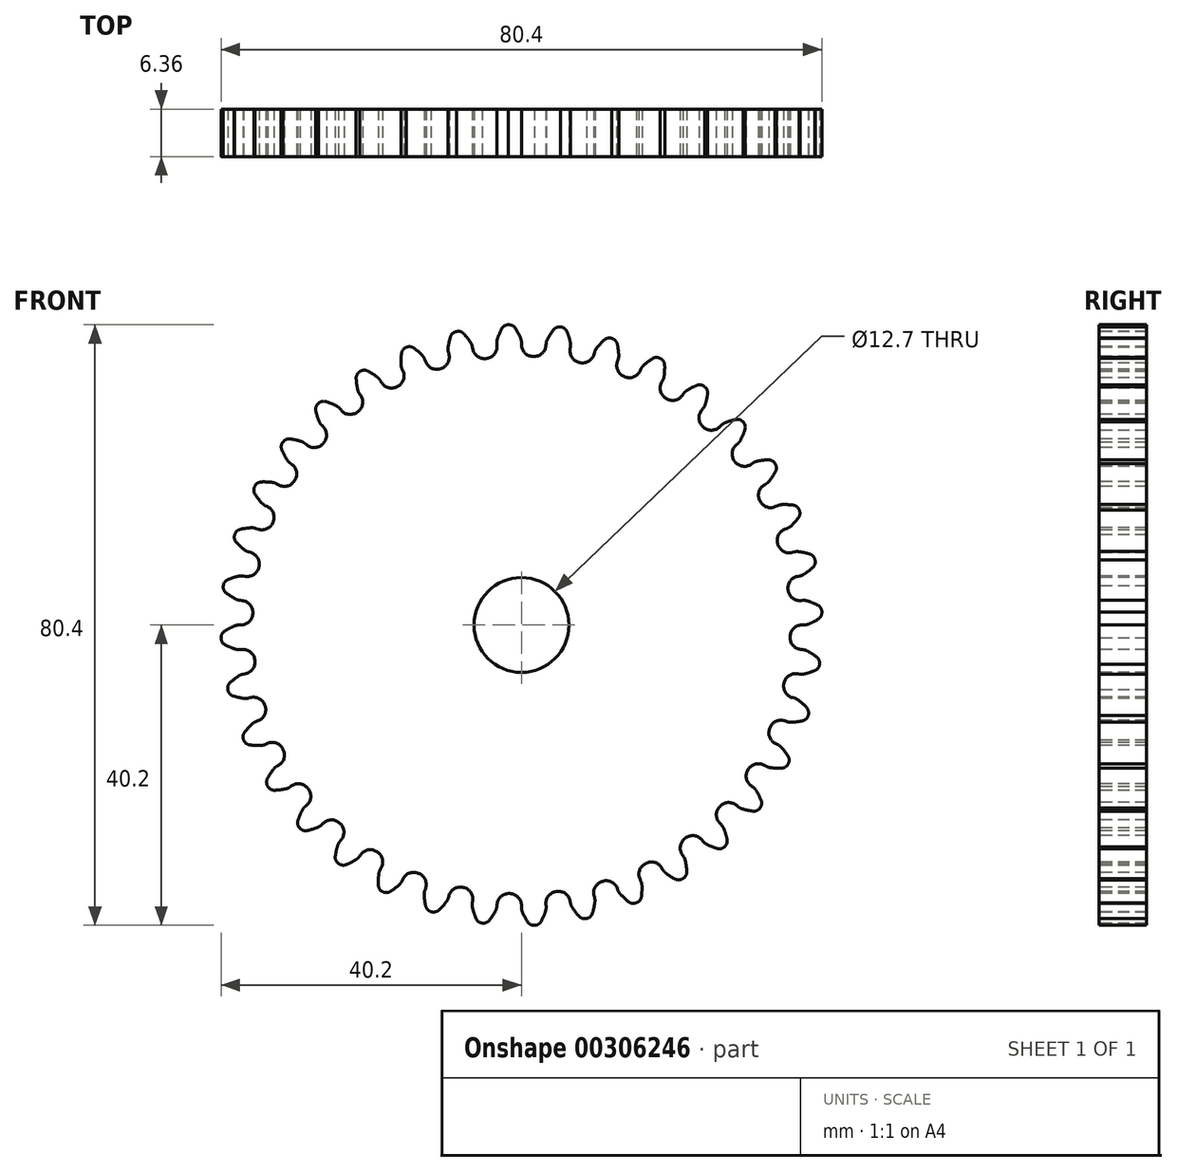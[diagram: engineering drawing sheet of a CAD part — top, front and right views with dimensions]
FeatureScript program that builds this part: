
annotation { "Feature Type Name" : "Feature", "Feature Type Description" : "" }
export const myFeature = defineFeature(function(context is Context, id is Id, definition is map)
    precondition{}
    {
        {
            var Q0;
            Q0=qCreatedBy(makeId("Front.planeOp"),FACE);
            var sketch = newSketch(context, id + "F0", { "sketchPlane" : qUnion([Q0])});
            skCircle(sketch, "E0", {"center": v(0, 0) * mm, "radius": 35.98 * mm});
            skSolve(sketch);
        }
        {
            var Q0;
            Q0 = qSketchRegion(id + "F0", true);
            extrude(context, id + "F1", {"entities" : qUnion([Q0]), "depth" : 3.17 * mm});
        }
        {
            var Q0;
            Q0=makeQuery(id+"F1.opExtrude","CAP_FACE",FACE,{"disambiguationData":[OSD([sQuery(id+"F0.wireOp",EDGE,"E0")])],"isStart":true});
            extrude(context, id + "F2", {"entities" : qUnion([Q0]), "operationType" : NewBodyOperationType.ADD, "depth" : 3.17 * mm});
        }
        {
            var Q0;
            Q0=makeQuery(id+"F1.opExtrude","CAP_FACE",FACE,{"disambiguationData":[OSD([sQuery(id+"F0.wireOp",EDGE,"E0")])],"isStart":false});
            var sketch = newSketch(context, id + "F3", { "sketchPlane" : qUnion([Q0])});
            skArc(sketch, "E1", {"start": v(-4.65, 35.68) * mm, "mid": v(1.57, -35.95) * mm, "end": v(1.52, 35.95) * mm});
            skArc(sketch, "E2.trimOffspring", {"start": v(-0.13, 38.41) * mm, "mid": v(-0.44, 39.08) * mm, "end": v(-0.8, 39.72) * mm});
            skLineSegment(sketch, "E3", {"start": v(-1.67, 40.2) * mm, "end": v(-1.76, 40.2) * mm});
            skLineSegment(sketch, "E4", {"start": v(0, 37.8) * mm, "end": v(0, 37.54) * mm});
            skLineSegment(sketch, "E5.MirrorCS", {"start": v(-1.84, 40.2) * mm, "end": v(-1.76, 40.2) * mm});
            skArc(sketch, "E6.MirrorCS", {"start": v(-3.22, 38.28) * mm, "mid": v(-2.97, 38.97) * mm, "end": v(-2.66, 39.64) * mm});
            skLineSegment(sketch, "E7.MirrorCS", {"start": v(-3.3, 37.65) * mm, "end": v(-3.27, 37.4) * mm});
            skPoint(sketch, "E8.orphan", {"position": v(-3.03, 34.61) * mm});
            skPoint(sketch, "E9.orphan", {"position": v(0, 34.74) * mm});
            skPoint(sketch, "E10.visualSharp", {"position": v(0, 35.98) * mm});
            skArc(sketch, "E10.filletArc", {"start": v(0, 36.45) * mm, "mid": v(0.13, 36.12) * mm, "end": v(0.46, 35.98) * mm});
            skArc(sketch, "E11.filletArc", {"start": v(0, 37.54) * mm, "mid": v(0.44, 36.44) * mm, "end": v(1.52, 35.95) * mm});
            skPoint(sketch, "E12.visualSharp", {"position": v(-3.14, 35.85) * mm});
            skArc(sketch, "E12.filletArc", {"start": v(-4.65, 35.68) * mm, "mid": v(-3.62, 36.26) * mm, "end": v(-3.27, 37.4) * mm});
            skPoint(sketch, "E13.visualSharp", {"position": v(0, 38.1) * mm});
            skArc(sketch, "E13.filletArc", {"start": v(0, 37.8) * mm, "mid": v(-0.03, 38.1) * mm, "end": v(-0.13, 38.41) * mm});
            skPoint(sketch, "E14.visualSharp", {"position": v(-3.32, 37.96) * mm});
            skArc(sketch, "E14.filletArc", {"start": v(-3.22, 38.28) * mm, "mid": v(-3.29, 37.97) * mm, "end": v(-3.3, 37.65) * mm});
            skPoint(sketch, "E15.visualSharp", {"position": v(-2.38, 40.15) * mm});
            skArc(sketch, "E15.filletArc", {"start": v(-1.84, 40.2) * mm, "mid": v(-2.32, 40.02) * mm, "end": v(-2.66, 39.64) * mm});
            skPoint(sketch, "E16.visualSharp", {"position": v(-1.13, 40.2) * mm});
            skArc(sketch, "E16.filletArc", {"start": v(-0.8, 39.72) * mm, "mid": v(-1.18, 40.07) * mm, "end": v(-1.67, 40.2) * mm});
            skArc(sketch, "E17.1.0", {"start": v(-6.52, 36.97) * mm, "mid": v(-5.9, 35.96) * mm, "end": v(-4.75, 35.67) * mm});
            skArc(sketch, "E17.1.1", {"start": v(-10.77, 34.33) * mm, "mid": v(-9.86, 35.08) * mm, "end": v(-9.72, 36.26) * mm});
            skArc(sketch, "E17.1.2", {"start": v(-8.8, 39.26) * mm, "mid": v(-9.23, 39.01) * mm, "end": v(-9.5, 38.58) * mm});
            skArc(sketch, "E17.1.3", {"start": v(-9.82, 37.14) * mm, "mid": v(-9.69, 37.86) * mm, "end": v(-9.5, 38.58) * mm});
            skPoint(sketch, "E17.1.4", {"position": v(-8.1, 39.4) * mm});
            skPoint(sketch, "E17.1.5", {"position": v(-6.62, 37.52) * mm});
            skPoint(sketch, "E17.1.6", {"position": v(-9.86, 36.8) * mm});
            skPoint(sketch, "E17.1.7", {"position": v(-9.32, 39.12) * mm});
            skArc(sketch, "E17.1.8", {"start": v(-6.8, 37.8) * mm, "mid": v(-7.22, 38.41) * mm, "end": v(-7.7, 38.98) * mm});
            skArc(sketch, "E17.1.9", {"start": v(-7.7, 38.98) * mm, "mid": v(-8.12, 39.26) * mm, "end": v(-8.63, 39.3) * mm});
            skArc(sketch, "E17.1.10", {"start": v(-6.56, 37.22) * mm, "mid": v(-6.65, 37.52) * mm, "end": v(-6.8, 37.8) * mm});
            skArc(sketch, "E17.1.11", {"start": v(-9.82, 37.14) * mm, "mid": v(-9.83, 36.82) * mm, "end": v(-9.78, 36.5) * mm});
            skLineSegment(sketch, "E17.1.12", {"start": v(-8.8, 39.26) * mm, "end": v(-8.7, 39.29) * mm});
            skLineSegment(sketch, "E17.1.13", {"start": v(-9.78, 36.5) * mm, "end": v(-9.72, 36.26) * mm});
            skLineSegment(sketch, "E17.1.14", {"start": v(-6.56, 37.22) * mm, "end": v(-6.52, 36.97) * mm});
            skLineSegment(sketch, "E17.1.15", {"start": v(-8.63, 39.3) * mm, "end": v(-8.7, 39.29) * mm});
            skArc(sketch, "E17.2.0", {"start": v(-12.84, 35.27) * mm, "mid": v(-12.05, 34.4) * mm, "end": v(-10.87, 34.3) * mm});
            skArc(sketch, "E17.2.1", {"start": v(-16.57, 31.94) * mm, "mid": v(-15.8, 32.84) * mm, "end": v(-15.86, 34.02) * mm});
            skArc(sketch, "E17.2.2", {"start": v(-15.48, 37.14) * mm, "mid": v(-15.87, 36.82) * mm, "end": v(-16.05, 36.34) * mm});
            skArc(sketch, "E17.2.3", {"start": v(-16.12, 34.87) * mm, "mid": v(-16.12, 35.6) * mm, "end": v(-16.05, 36.34) * mm});
            skPoint(sketch, "E17.2.4", {"position": v(-14.8, 37.4) * mm});
            skPoint(sketch, "E17.2.5", {"position": v(-13.03, 35.8) * mm});
            skPoint(sketch, "E17.2.6", {"position": v(-16.1, 34.53) * mm});
            skPoint(sketch, "E17.2.7", {"position": v(-15.97, 36.91) * mm});
            skArc(sketch, "E17.2.8", {"start": v(-13.26, 36.05) * mm, "mid": v(-13.78, 36.57) * mm, "end": v(-14.35, 37.05) * mm});
            skArc(sketch, "E17.2.9", {"start": v(-14.35, 37.05) * mm, "mid": v(-14.81, 37.25) * mm, "end": v(-15.32, 37.2) * mm});
            skArc(sketch, "E17.2.10", {"start": v(-12.93, 35.51) * mm, "mid": v(-13.06, 35.8) * mm, "end": v(-13.26, 36.05) * mm});
            skArc(sketch, "E17.2.11", {"start": v(-16.12, 34.87) * mm, "mid": v(-16.08, 34.55) * mm, "end": v(-15.97, 34.25) * mm});
            skLineSegment(sketch, "E17.2.12", {"start": v(-15.48, 37.14) * mm, "end": v(-15.4, 37.18) * mm});
            skLineSegment(sketch, "E17.2.13", {"start": v(-15.97, 34.25) * mm, "end": v(-15.86, 34.02) * mm});
            skLineSegment(sketch, "E17.2.14", {"start": v(-12.93, 35.51) * mm, "end": v(-12.84, 35.27) * mm});
            skLineSegment(sketch, "E17.2.15", {"start": v(-15.32, 37.2) * mm, "end": v(-15.4, 37.18) * mm});
            skArc(sketch, "E18.3.3.0", {"start": v(-18.77, 32.5) * mm, "mid": v(-17.84, 31.78) * mm, "end": v(-16.66, 31.9) * mm});
            skArc(sketch, "E18.4.3.0", {"start": v(-21.87, 28.58) * mm, "mid": v(-21.26, 29.6) * mm, "end": v(-21.53, 30.75) * mm});
            skArc(sketch, "E18.8.3.0", {"start": v(-21.69, 33.89) * mm, "mid": v(-22.02, 33.5) * mm, "end": v(-22.12, 33) * mm});
            skArc(sketch, "E18.12.3.0", {"start": v(-21.93, 31.54) * mm, "mid": v(-22.05, 32.27) * mm, "end": v(-22.12, 33) * mm});
            skPoint(sketch, "E18.16.3.0", {"position": v(-21.08, 34.25) * mm});
            skPoint(sketch, "E18.17.3.0", {"position": v(-19.05, 33) * mm});
            skPoint(sketch, "E18.18.3.0", {"position": v(-21.85, 31.2) * mm});
            skPoint(sketch, "E18.19.3.0", {"position": v(-22.13, 33.58) * mm});
            skArc(sketch, "E18.20.3.0", {"start": v(-19.32, 33.2) * mm, "mid": v(-19.92, 33.62) * mm, "end": v(-20.56, 34) * mm});
            skArc(sketch, "E18.24.3.0", {"start": v(-20.56, 34) * mm, "mid": v(-21.06, 34.12) * mm, "end": v(-21.55, 33.98) * mm});
            skArc(sketch, "E18.28.3.0", {"start": v(-18.9, 32.73) * mm, "mid": v(-19.08, 32.99) * mm, "end": v(-19.32, 33.2) * mm});
            skArc(sketch, "E18.32.3.0", {"start": v(-21.93, 31.54) * mm, "mid": v(-21.83, 31.24) * mm, "end": v(-21.68, 30.96) * mm});
            skLineSegment(sketch, "E18.36.3.0", {"start": v(-21.69, 33.89) * mm, "end": v(-21.62, 33.94) * mm});
            skLineSegment(sketch, "E18.39.3.0", {"start": v(-21.68, 30.96) * mm, "end": v(-21.53, 30.75) * mm});
            skLineSegment(sketch, "E18.42.3.0", {"start": v(-18.9, 32.73) * mm, "end": v(-18.77, 32.5) * mm});
            skLineSegment(sketch, "E18.45.3.0", {"start": v(-21.55, 33.98) * mm, "end": v(-21.62, 33.94) * mm});
            skArc(sketch, "E18.3.4.0", {"start": v(-24.13, 28.76) * mm, "mid": v(-23.08, 28.2) * mm, "end": v(-21.94, 28.52) * mm});
            skArc(sketch, "E18.4.4.0", {"start": v(-26.5, 24.35) * mm, "mid": v(-26.08, 25.45) * mm, "end": v(-26.54, 26.54) * mm});
            skArc(sketch, "E18.8.4.0", {"start": v(-27.24, 29.6) * mm, "mid": v(-27.5, 29.17) * mm, "end": v(-27.52, 28.66) * mm});
            skArc(sketch, "E18.12.4.0", {"start": v(-27.07, 27.25) * mm, "mid": v(-27.32, 27.95) * mm, "end": v(-27.52, 28.66) * mm});
            skPoint(sketch, "E18.16.4.0", {"position": v(-26.7, 30.07) * mm});
            skPoint(sketch, "E18.17.4.0", {"position": v(-24.5, 29.19) * mm});
            skPoint(sketch, "E18.18.4.0", {"position": v(-26.94, 26.94) * mm});
            skPoint(sketch, "E18.19.4.0", {"position": v(-27.63, 29.22) * mm});
            skArc(sketch, "E18.20.4.0", {"start": v(-24.79, 29.34) * mm, "mid": v(-25.46, 29.65) * mm, "end": v(-26.15, 29.9) * mm});
            skArc(sketch, "E18.24.4.0", {"start": v(-26.15, 29.9) * mm, "mid": v(-26.66, 29.94) * mm, "end": v(-27.12, 29.72) * mm});
            skArc(sketch, "E18.28.4.0", {"start": v(-24.3, 28.95) * mm, "mid": v(-24.52, 29.17) * mm, "end": v(-24.79, 29.34) * mm});
            skArc(sketch, "E18.32.4.0", {"start": v(-27.07, 27.25) * mm, "mid": v(-26.92, 26.97) * mm, "end": v(-26.72, 26.72) * mm});
            skLineSegment(sketch, "E18.36.4.0", {"start": v(-27.24, 29.6) * mm, "end": v(-27.19, 29.67) * mm});
            skLineSegment(sketch, "E18.39.4.0", {"start": v(-26.72, 26.72) * mm, "end": v(-26.54, 26.54) * mm});
            skLineSegment(sketch, "E18.42.4.0", {"start": v(-24.3, 28.95) * mm, "end": v(-24.13, 28.76) * mm});
            skLineSegment(sketch, "E18.45.4.0", {"start": v(-27.12, 29.72) * mm, "end": v(-27.19, 29.67) * mm});
            skArc(sketch, "E18.3.5.0", {"start": v(-28.76, 24.13) * mm, "mid": v(-27.63, 23.76) * mm, "end": v(-26.56, 24.27) * mm});
            skArc(sketch, "E18.4.5.0", {"start": v(-30.32, 19.38) * mm, "mid": v(-30.1, 20.54) * mm, "end": v(-30.75, 21.53) * mm});
            skArc(sketch, "E18.8.5.0", {"start": v(-31.97, 24.43) * mm, "mid": v(-32.15, 23.95) * mm, "end": v(-32.07, 23.45) * mm});
            skArc(sketch, "E18.12.5.0", {"start": v(-31.4, 22.14) * mm, "mid": v(-31.76, 22.78) * mm, "end": v(-32.07, 23.45) * mm});
            skPoint(sketch, "E18.16.5.0", {"position": v(-31.52, 24.98) * mm});
            skPoint(sketch, "E18.17.5.0", {"position": v(-29.19, 24.5) * mm});
            skPoint(sketch, "E18.18.5.0", {"position": v(-31.2, 21.85) * mm});
            skPoint(sketch, "E18.19.5.0", {"position": v(-32.28, 23.98) * mm});
            skArc(sketch, "E18.20.5.0", {"start": v(-29.5, 24.6) * mm, "mid": v(-30.22, 24.78) * mm, "end": v(-30.95, 24.91) * mm});
            skArc(sketch, "E18.24.5.0", {"start": v(-30.95, 24.91) * mm, "mid": v(-31.46, 24.86) * mm, "end": v(-31.87, 24.56) * mm});
            skArc(sketch, "E18.28.5.0", {"start": v(-28.95, 24.3) * mm, "mid": v(-29.21, 24.47) * mm, "end": v(-29.5, 24.6) * mm});
            skArc(sketch, "E18.32.5.0", {"start": v(-31.4, 22.14) * mm, "mid": v(-31.2, 21.88) * mm, "end": v(-30.96, 21.68) * mm});
            skLineSegment(sketch, "E18.36.5.0", {"start": v(-31.97, 24.43) * mm, "end": v(-31.92, 24.5) * mm});
            skLineSegment(sketch, "E18.39.5.0", {"start": v(-30.96, 21.68) * mm, "end": v(-30.75, 21.53) * mm});
            skLineSegment(sketch, "E18.42.5.0", {"start": v(-28.95, 24.3) * mm, "end": v(-28.76, 24.13) * mm});
            skLineSegment(sketch, "E18.45.5.0", {"start": v(-31.87, 24.56) * mm, "end": v(-31.92, 24.5) * mm});
            skArc(sketch, "E18.3.6.0", {"start": v(-32.5, 18.77) * mm, "mid": v(-31.34, 18.6) * mm, "end": v(-30.37, 19.3) * mm});
            skArc(sketch, "E18.4.6.0", {"start": v(-33.23, 13.82) * mm, "mid": v(-33.21, 15) * mm, "end": v(-34.02, 15.86) * mm});
            skArc(sketch, "E18.8.6.0", {"start": v(-35.73, 18.5) * mm, "mid": v(-35.82, 18) * mm, "end": v(-35.66, 17.52) * mm});
            skArc(sketch, "E18.12.6.0", {"start": v(-34.76, 16.35) * mm, "mid": v(-35.23, 16.92) * mm, "end": v(-35.66, 17.52) * mm});
            skPoint(sketch, "E18.16.6.0", {"position": v(-35.38, 19.12) * mm});
            skPoint(sketch, "E18.17.6.0", {"position": v(-33, 19.05) * mm});
            skPoint(sketch, "E18.18.6.0", {"position": v(-34.53, 16.1) * mm});
            skPoint(sketch, "E18.19.6.0", {"position": v(-35.96, 18.01) * mm});
            skArc(sketch, "E18.20.6.0", {"start": v(-33.33, 19.1) * mm, "mid": v(-34.07, 19.16) * mm, "end": v(-34.8, 19.16) * mm});
            skArc(sketch, "E18.24.6.0", {"start": v(-34.8, 19.16) * mm, "mid": v(-35.3, 19.02) * mm, "end": v(-35.65, 18.65) * mm});
            skArc(sketch, "E18.28.6.0", {"start": v(-32.73, 18.9) * mm, "mid": v(-33.02, 19.03) * mm, "end": v(-33.33, 19.1) * mm});
            skArc(sketch, "E18.32.6.0", {"start": v(-34.76, 16.35) * mm, "mid": v(-34.52, 16.13) * mm, "end": v(-34.25, 15.97) * mm});
            skLineSegment(sketch, "E18.36.6.0", {"start": v(-35.73, 18.5) * mm, "end": v(-35.7, 18.58) * mm});
            skLineSegment(sketch, "E18.39.6.0", {"start": v(-34.25, 15.97) * mm, "end": v(-34.02, 15.86) * mm});
            skLineSegment(sketch, "E18.42.6.0", {"start": v(-32.73, 18.9) * mm, "end": v(-32.5, 18.77) * mm});
            skLineSegment(sketch, "E18.45.6.0", {"start": v(-35.65, 18.65) * mm, "end": v(-35.7, 18.58) * mm});
            skArc(sketch, "E18.3.7.0", {"start": v(-35.27, 12.84) * mm, "mid": v(-34.1, 12.88) * mm, "end": v(-33.26, 13.72) * mm});
            skArc(sketch, "E18.4.7.0", {"start": v(-35.12, 7.84) * mm, "mid": v(-35.31, 9) * mm, "end": v(-36.26, 9.72) * mm});
            skArc(sketch, "E18.8.7.0", {"start": v(-38.4, 12.02) * mm, "mid": v(-38.4, 11.5) * mm, "end": v(-38.16, 11.06) * mm});
            skArc(sketch, "E18.12.7.0", {"start": v(-37.07, 10.06) * mm, "mid": v(-37.64, 10.54) * mm, "end": v(-38.16, 11.06) * mm});
            skPoint(sketch, "E18.16.7.0", {"position": v(-38.16, 12.69) * mm});
            skPoint(sketch, "E18.17.7.0", {"position": v(-35.8, 13.03) * mm});
            skPoint(sketch, "E18.18.7.0", {"position": v(-36.8, 9.86) * mm});
            skPoint(sketch, "E18.19.7.0", {"position": v(-38.54, 11.5) * mm});
            skArc(sketch, "E18.20.7.0", {"start": v(-36.14, 13.02) * mm, "mid": v(-36.88, 12.95) * mm, "end": v(-37.6, 12.83) * mm});
            skArc(sketch, "E18.24.7.0", {"start": v(-37.6, 12.83) * mm, "mid": v(-38.06, 12.6) * mm, "end": v(-38.35, 12.18) * mm});
            skArc(sketch, "E18.28.7.0", {"start": v(-35.51, 12.93) * mm, "mid": v(-35.82, 13) * mm, "end": v(-36.14, 13.02) * mm});
            skArc(sketch, "E18.32.7.0", {"start": v(-37.07, 10.06) * mm, "mid": v(-36.8, 9.9) * mm, "end": v(-36.5, 9.78) * mm});
            skLineSegment(sketch, "E18.36.7.0", {"start": v(-38.4, 12.02) * mm, "end": v(-38.38, 12.1) * mm});
            skLineSegment(sketch, "E18.39.7.0", {"start": v(-36.5, 9.78) * mm, "end": v(-36.26, 9.72) * mm});
            skLineSegment(sketch, "E18.42.7.0", {"start": v(-35.51, 12.93) * mm, "end": v(-35.27, 12.84) * mm});
            skLineSegment(sketch, "E18.45.7.0", {"start": v(-38.35, 12.18) * mm, "end": v(-38.38, 12.1) * mm});
            skArc(sketch, "E18.3.8.0", {"start": v(-36.97, 6.52) * mm, "mid": v(-35.8, 6.76) * mm, "end": v(-35.14, 7.74) * mm});
            skArc(sketch, "E18.4.8.0", {"start": v(-35.95, 1.62) * mm, "mid": v(-36.34, 2.74) * mm, "end": v(-37.4, 3.27) * mm});
            skArc(sketch, "E18.8.8.0", {"start": v(-39.9, 5.17) * mm, "mid": v(-39.82, 4.67) * mm, "end": v(-39.5, 4.27) * mm});
            skArc(sketch, "E18.12.8.0", {"start": v(-38.26, 3.47) * mm, "mid": v(-38.9, 3.85) * mm, "end": v(-39.5, 4.27) * mm});
            skPoint(sketch, "E18.16.8.0", {"position": v(-39.79, 5.87) * mm});
            skPoint(sketch, "E18.17.8.0", {"position": v(-37.52, 6.62) * mm});
            skPoint(sketch, "E18.18.8.0", {"position": v(-37.96, 3.32) * mm});
            skPoint(sketch, "E18.19.8.0", {"position": v(-39.95, 4.63) * mm});
            skArc(sketch, "E18.20.8.0", {"start": v(-37.85, 6.55) * mm, "mid": v(-38.56, 6.35) * mm, "end": v(-39.26, 6.1) * mm});
            skArc(sketch, "E18.24.8.0", {"start": v(-39.26, 6.1) * mm, "mid": v(-39.67, 5.8) * mm, "end": v(-39.88, 5.34) * mm});
            skArc(sketch, "E18.28.8.0", {"start": v(-37.22, 6.56) * mm, "mid": v(-37.54, 6.59) * mm, "end": v(-37.85, 6.55) * mm});
            skArc(sketch, "E18.32.8.0", {"start": v(-38.26, 3.47) * mm, "mid": v(-37.96, 3.35) * mm, "end": v(-37.65, 3.3) * mm});
            skLineSegment(sketch, "E18.36.8.0", {"start": v(-39.9, 5.17) * mm, "end": v(-39.9, 5.25) * mm});
            skLineSegment(sketch, "E18.39.8.0", {"start": v(-37.65, 3.3) * mm, "end": v(-37.4, 3.27) * mm});
            skLineSegment(sketch, "E18.42.8.0", {"start": v(-37.22, 6.56) * mm, "end": v(-36.97, 6.52) * mm});
            skLineSegment(sketch, "E18.45.8.0", {"start": v(-39.88, 5.34) * mm, "end": v(-39.9, 5.25) * mm});
            skArc(sketch, "E18.3.9.0", {"start": v(-37.54, 0) * mm, "mid": v(-36.44, 0.44) * mm, "end": v(-35.95, 1.52) * mm});
            skArc(sketch, "E18.4.9.0", {"start": v(-35.68, -4.65) * mm, "mid": v(-36.26, -3.62) * mm, "end": v(-37.4, -3.27) * mm});
            skArc(sketch, "E18.8.9.0", {"start": v(-40.2, -1.84) * mm, "mid": v(-40.02, -2.32) * mm, "end": v(-39.64, -2.66) * mm});
            skArc(sketch, "E18.12.9.0", {"start": v(-38.28, -3.22) * mm, "mid": v(-38.97, -2.97) * mm, "end": v(-39.64, -2.66) * mm});
            skPoint(sketch, "E18.16.9.0", {"position": v(-40.2, -1.13) * mm});
            skPoint(sketch, "E18.17.9.0", {"position": v(-38.1, 0) * mm});
            skPoint(sketch, "E18.18.9.0", {"position": v(-37.96, -3.32) * mm});
            skPoint(sketch, "E18.19.9.0", {"position": v(-40.15, -2.38) * mm});
            skArc(sketch, "E18.20.9.0", {"start": v(-38.41, -0.13) * mm, "mid": v(-39.08, -0.44) * mm, "end": v(-39.72, -0.8) * mm});
            skArc(sketch, "E18.24.9.0", {"start": v(-39.72, -0.8) * mm, "mid": v(-40.07, -1.18) * mm, "end": v(-40.2, -1.67) * mm});
            skArc(sketch, "E18.28.9.0", {"start": v(-37.8, 0) * mm, "mid": v(-38.1, -0.03) * mm, "end": v(-38.41, -0.13) * mm});
            skArc(sketch, "E18.32.9.0", {"start": v(-38.28, -3.22) * mm, "mid": v(-37.97, -3.29) * mm, "end": v(-37.65, -3.3) * mm});
            skLineSegment(sketch, "E18.36.9.0", {"start": v(-40.2, -1.84) * mm, "end": v(-40.2, -1.76) * mm});
            skLineSegment(sketch, "E18.39.9.0", {"start": v(-37.65, -3.3) * mm, "end": v(-37.4, -3.27) * mm});
            skLineSegment(sketch, "E18.42.9.0", {"start": v(-37.8, 0) * mm, "end": v(-37.54, 0) * mm});
            skLineSegment(sketch, "E18.45.9.0", {"start": v(-40.2, -1.67) * mm, "end": v(-40.2, -1.76) * mm});
            skArc(sketch, "E18.3.10.0", {"start": v(-36.97, -6.52) * mm, "mid": v(-35.96, -5.9) * mm, "end": v(-35.67, -4.75) * mm});
            skArc(sketch, "E18.4.10.0", {"start": v(-34.33, -10.77) * mm, "mid": v(-35.08, -9.86) * mm, "end": v(-36.26, -9.72) * mm});
            skArc(sketch, "E18.8.10.0", {"start": v(-39.26, -8.8) * mm, "mid": v(-39.01, -9.23) * mm, "end": v(-38.58, -9.5) * mm});
            skArc(sketch, "E18.12.10.0", {"start": v(-37.14, -9.82) * mm, "mid": v(-37.86, -9.69) * mm, "end": v(-38.58, -9.5) * mm});
            skPoint(sketch, "E18.16.10.0", {"position": v(-39.4, -8.1) * mm});
            skPoint(sketch, "E18.17.10.0", {"position": v(-37.52, -6.62) * mm});
            skPoint(sketch, "E18.18.10.0", {"position": v(-36.8, -9.86) * mm});
            skPoint(sketch, "E18.19.10.0", {"position": v(-39.12, -9.32) * mm});
            skArc(sketch, "E18.20.10.0", {"start": v(-37.8, -6.8) * mm, "mid": v(-38.41, -7.22) * mm, "end": v(-38.98, -7.7) * mm});
            skArc(sketch, "E18.24.10.0", {"start": v(-38.98, -7.7) * mm, "mid": v(-39.26, -8.12) * mm, "end": v(-39.3, -8.63) * mm});
            skArc(sketch, "E18.28.10.0", {"start": v(-37.22, -6.56) * mm, "mid": v(-37.52, -6.65) * mm, "end": v(-37.8, -6.8) * mm});
            skArc(sketch, "E18.32.10.0", {"start": v(-37.14, -9.82) * mm, "mid": v(-36.82, -9.83) * mm, "end": v(-36.5, -9.78) * mm});
            skLineSegment(sketch, "E18.36.10.0", {"start": v(-39.26, -8.8) * mm, "end": v(-39.29, -8.7) * mm});
            skLineSegment(sketch, "E18.39.10.0", {"start": v(-36.5, -9.78) * mm, "end": v(-36.26, -9.72) * mm});
            skLineSegment(sketch, "E18.42.10.0", {"start": v(-37.22, -6.56) * mm, "end": v(-36.97, -6.52) * mm});
            skLineSegment(sketch, "E18.45.10.0", {"start": v(-39.3, -8.63) * mm, "end": v(-39.29, -8.7) * mm});
            skArc(sketch, "E18.3.11.0", {"start": v(-35.27, -12.84) * mm, "mid": v(-34.4, -12.05) * mm, "end": v(-34.3, -10.87) * mm});
            skArc(sketch, "E18.4.11.0", {"start": v(-31.94, -16.57) * mm, "mid": v(-32.84, -15.8) * mm, "end": v(-34.02, -15.86) * mm});
            skArc(sketch, "E18.8.11.0", {"start": v(-37.14, -15.48) * mm, "mid": v(-36.82, -15.87) * mm, "end": v(-36.34, -16.05) * mm});
            skArc(sketch, "E18.12.11.0", {"start": v(-34.87, -16.12) * mm, "mid": v(-35.6, -16.12) * mm, "end": v(-36.34, -16.05) * mm});
            skPoint(sketch, "E18.16.11.0", {"position": v(-37.4, -14.8) * mm});
            skPoint(sketch, "E18.17.11.0", {"position": v(-35.8, -13.03) * mm});
            skPoint(sketch, "E18.18.11.0", {"position": v(-34.53, -16.1) * mm});
            skPoint(sketch, "E18.19.11.0", {"position": v(-36.91, -15.97) * mm});
            skArc(sketch, "E18.20.11.0", {"start": v(-36.05, -13.26) * mm, "mid": v(-36.57, -13.78) * mm, "end": v(-37.05, -14.35) * mm});
            skArc(sketch, "E18.24.11.0", {"start": v(-37.05, -14.35) * mm, "mid": v(-37.25, -14.81) * mm, "end": v(-37.2, -15.32) * mm});
            skArc(sketch, "E18.28.11.0", {"start": v(-35.51, -12.93) * mm, "mid": v(-35.8, -13.06) * mm, "end": v(-36.05, -13.26) * mm});
            skArc(sketch, "E18.32.11.0", {"start": v(-34.87, -16.12) * mm, "mid": v(-34.55, -16.08) * mm, "end": v(-34.25, -15.97) * mm});
            skLineSegment(sketch, "E18.36.11.0", {"start": v(-37.14, -15.48) * mm, "end": v(-37.18, -15.4) * mm});
            skLineSegment(sketch, "E18.39.11.0", {"start": v(-34.25, -15.97) * mm, "end": v(-34.02, -15.86) * mm});
            skLineSegment(sketch, "E18.42.11.0", {"start": v(-35.51, -12.93) * mm, "end": v(-35.27, -12.84) * mm});
            skLineSegment(sketch, "E18.45.11.0", {"start": v(-37.2, -15.32) * mm, "end": v(-37.18, -15.4) * mm});
            skArc(sketch, "E18.3.12.0", {"start": v(-32.5, -18.77) * mm, "mid": v(-31.78, -17.84) * mm, "end": v(-31.9, -16.66) * mm});
            skArc(sketch, "E18.4.12.0", {"start": v(-28.58, -21.87) * mm, "mid": v(-29.6, -21.26) * mm, "end": v(-30.75, -21.53) * mm});
            skArc(sketch, "E18.8.12.0", {"start": v(-33.89, -21.69) * mm, "mid": v(-33.5, -22.02) * mm, "end": v(-33, -22.12) * mm});
            skArc(sketch, "E18.12.12.0", {"start": v(-31.54, -21.93) * mm, "mid": v(-32.27, -22.05) * mm, "end": v(-33, -22.12) * mm});
            skPoint(sketch, "E18.16.12.0", {"position": v(-34.25, -21.08) * mm});
            skPoint(sketch, "E18.17.12.0", {"position": v(-33, -19.05) * mm});
            skPoint(sketch, "E18.18.12.0", {"position": v(-31.2, -21.85) * mm});
            skPoint(sketch, "E18.19.12.0", {"position": v(-33.58, -22.13) * mm});
            skArc(sketch, "E18.20.12.0", {"start": v(-33.2, -19.32) * mm, "mid": v(-33.62, -19.92) * mm, "end": v(-34, -20.56) * mm});
            skArc(sketch, "E18.24.12.0", {"start": v(-34, -20.56) * mm, "mid": v(-34.12, -21.06) * mm, "end": v(-33.98, -21.55) * mm});
            skArc(sketch, "E18.28.12.0", {"start": v(-32.73, -18.9) * mm, "mid": v(-32.99, -19.08) * mm, "end": v(-33.2, -19.32) * mm});
            skArc(sketch, "E18.32.12.0", {"start": v(-31.54, -21.93) * mm, "mid": v(-31.24, -21.83) * mm, "end": v(-30.96, -21.68) * mm});
            skLineSegment(sketch, "E18.36.12.0", {"start": v(-33.89, -21.69) * mm, "end": v(-33.94, -21.62) * mm});
            skLineSegment(sketch, "E18.39.12.0", {"start": v(-30.96, -21.68) * mm, "end": v(-30.75, -21.53) * mm});
            skLineSegment(sketch, "E18.42.12.0", {"start": v(-32.73, -18.9) * mm, "end": v(-32.5, -18.77) * mm});
            skLineSegment(sketch, "E18.45.12.0", {"start": v(-33.98, -21.55) * mm, "end": v(-33.94, -21.62) * mm});
            skArc(sketch, "E18.3.13.0", {"start": v(-28.76, -24.13) * mm, "mid": v(-28.2, -23.08) * mm, "end": v(-28.52, -21.94) * mm});
            skArc(sketch, "E18.4.13.0", {"start": v(-24.35, -26.5) * mm, "mid": v(-25.45, -26.08) * mm, "end": v(-26.54, -26.54) * mm});
            skArc(sketch, "E18.8.13.0", {"start": v(-29.6, -27.24) * mm, "mid": v(-29.17, -27.5) * mm, "end": v(-28.66, -27.52) * mm});
            skArc(sketch, "E18.12.13.0", {"start": v(-27.25, -27.07) * mm, "mid": v(-27.95, -27.32) * mm, "end": v(-28.66, -27.52) * mm});
            skPoint(sketch, "E18.16.13.0", {"position": v(-30.07, -26.7) * mm});
            skPoint(sketch, "E18.17.13.0", {"position": v(-29.19, -24.5) * mm});
            skPoint(sketch, "E18.18.13.0", {"position": v(-26.94, -26.94) * mm});
            skPoint(sketch, "E18.19.13.0", {"position": v(-29.22, -27.63) * mm});
            skArc(sketch, "E18.20.13.0", {"start": v(-29.34, -24.79) * mm, "mid": v(-29.65, -25.46) * mm, "end": v(-29.9, -26.15) * mm});
            skArc(sketch, "E18.24.13.0", {"start": v(-29.9, -26.15) * mm, "mid": v(-29.94, -26.66) * mm, "end": v(-29.72, -27.12) * mm});
            skArc(sketch, "E18.28.13.0", {"start": v(-28.95, -24.3) * mm, "mid": v(-29.17, -24.52) * mm, "end": v(-29.34, -24.79) * mm});
            skArc(sketch, "E18.32.13.0", {"start": v(-27.25, -27.07) * mm, "mid": v(-26.97, -26.92) * mm, "end": v(-26.72, -26.72) * mm});
            skLineSegment(sketch, "E18.36.13.0", {"start": v(-29.6, -27.24) * mm, "end": v(-29.67, -27.19) * mm});
            skLineSegment(sketch, "E18.39.13.0", {"start": v(-26.72, -26.72) * mm, "end": v(-26.54, -26.54) * mm});
            skLineSegment(sketch, "E18.42.13.0", {"start": v(-28.95, -24.3) * mm, "end": v(-28.76, -24.13) * mm});
            skLineSegment(sketch, "E18.45.13.0", {"start": v(-29.72, -27.12) * mm, "end": v(-29.67, -27.19) * mm});
            skArc(sketch, "E18.3.14.0", {"start": v(-24.13, -28.76) * mm, "mid": v(-23.76, -27.63) * mm, "end": v(-24.27, -26.56) * mm});
            skArc(sketch, "E18.4.14.0", {"start": v(-19.38, -30.32) * mm, "mid": v(-20.54, -30.1) * mm, "end": v(-21.53, -30.75) * mm});
            skArc(sketch, "E18.8.14.0", {"start": v(-24.43, -31.97) * mm, "mid": v(-23.95, -32.15) * mm, "end": v(-23.45, -32.07) * mm});
            skArc(sketch, "E18.12.14.0", {"start": v(-22.14, -31.4) * mm, "mid": v(-22.78, -31.76) * mm, "end": v(-23.45, -32.07) * mm});
            skPoint(sketch, "E18.16.14.0", {"position": v(-24.98, -31.52) * mm});
            skPoint(sketch, "E18.17.14.0", {"position": v(-24.5, -29.19) * mm});
            skPoint(sketch, "E18.18.14.0", {"position": v(-21.85, -31.2) * mm});
            skPoint(sketch, "E18.19.14.0", {"position": v(-23.98, -32.28) * mm});
            skArc(sketch, "E18.20.14.0", {"start": v(-24.6, -29.5) * mm, "mid": v(-24.78, -30.22) * mm, "end": v(-24.91, -30.95) * mm});
            skArc(sketch, "E18.24.14.0", {"start": v(-24.91, -30.95) * mm, "mid": v(-24.86, -31.46) * mm, "end": v(-24.56, -31.87) * mm});
            skArc(sketch, "E18.28.14.0", {"start": v(-24.3, -28.95) * mm, "mid": v(-24.47, -29.21) * mm, "end": v(-24.6, -29.5) * mm});
            skArc(sketch, "E18.32.14.0", {"start": v(-22.14, -31.4) * mm, "mid": v(-21.88, -31.2) * mm, "end": v(-21.68, -30.96) * mm});
            skLineSegment(sketch, "E18.36.14.0", {"start": v(-24.43, -31.97) * mm, "end": v(-24.5, -31.92) * mm});
            skLineSegment(sketch, "E18.39.14.0", {"start": v(-21.68, -30.96) * mm, "end": v(-21.53, -30.75) * mm});
            skLineSegment(sketch, "E18.42.14.0", {"start": v(-24.3, -28.95) * mm, "end": v(-24.13, -28.76) * mm});
            skLineSegment(sketch, "E18.45.14.0", {"start": v(-24.56, -31.87) * mm, "end": v(-24.5, -31.92) * mm});
            skArc(sketch, "E18.3.15.0", {"start": v(-18.77, -32.5) * mm, "mid": v(-18.6, -31.34) * mm, "end": v(-19.3, -30.37) * mm});
            skArc(sketch, "E18.4.15.0", {"start": v(-13.82, -33.23) * mm, "mid": v(-15, -33.21) * mm, "end": v(-15.86, -34.02) * mm});
            skArc(sketch, "E18.8.15.0", {"start": v(-18.5, -35.73) * mm, "mid": v(-18, -35.82) * mm, "end": v(-17.52, -35.66) * mm});
            skArc(sketch, "E18.12.15.0", {"start": v(-16.35, -34.76) * mm, "mid": v(-16.92, -35.23) * mm, "end": v(-17.52, -35.66) * mm});
            skPoint(sketch, "E18.16.15.0", {"position": v(-19.12, -35.38) * mm});
            skPoint(sketch, "E18.17.15.0", {"position": v(-19.05, -33) * mm});
            skPoint(sketch, "E18.18.15.0", {"position": v(-16.1, -34.53) * mm});
            skPoint(sketch, "E18.19.15.0", {"position": v(-18.01, -35.96) * mm});
            skArc(sketch, "E18.20.15.0", {"start": v(-19.1, -33.33) * mm, "mid": v(-19.16, -34.07) * mm, "end": v(-19.16, -34.8) * mm});
            skArc(sketch, "E18.24.15.0", {"start": v(-19.16, -34.8) * mm, "mid": v(-19.02, -35.3) * mm, "end": v(-18.65, -35.65) * mm});
            skArc(sketch, "E18.28.15.0", {"start": v(-18.9, -32.73) * mm, "mid": v(-19.03, -33.02) * mm, "end": v(-19.1, -33.33) * mm});
            skArc(sketch, "E18.32.15.0", {"start": v(-16.35, -34.76) * mm, "mid": v(-16.13, -34.52) * mm, "end": v(-15.97, -34.25) * mm});
            skLineSegment(sketch, "E18.36.15.0", {"start": v(-18.5, -35.73) * mm, "end": v(-18.58, -35.7) * mm});
            skLineSegment(sketch, "E18.39.15.0", {"start": v(-15.97, -34.25) * mm, "end": v(-15.86, -34.02) * mm});
            skLineSegment(sketch, "E18.42.15.0", {"start": v(-18.9, -32.73) * mm, "end": v(-18.77, -32.5) * mm});
            skLineSegment(sketch, "E18.45.15.0", {"start": v(-18.65, -35.65) * mm, "end": v(-18.58, -35.7) * mm});
            skArc(sketch, "E18.3.16.0", {"start": v(-12.84, -35.27) * mm, "mid": v(-12.88, -34.1) * mm, "end": v(-13.72, -33.26) * mm});
            skArc(sketch, "E18.4.16.0", {"start": v(-7.84, -35.12) * mm, "mid": v(-9, -35.31) * mm, "end": v(-9.72, -36.26) * mm});
            skArc(sketch, "E18.8.16.0", {"start": v(-12.02, -38.4) * mm, "mid": v(-11.5, -38.4) * mm, "end": v(-11.06, -38.16) * mm});
            skArc(sketch, "E18.12.16.0", {"start": v(-10.06, -37.07) * mm, "mid": v(-10.54, -37.64) * mm, "end": v(-11.06, -38.16) * mm});
            skPoint(sketch, "E18.16.16.0", {"position": v(-12.69, -38.16) * mm});
            skPoint(sketch, "E18.17.16.0", {"position": v(-13.03, -35.8) * mm});
            skPoint(sketch, "E18.18.16.0", {"position": v(-9.86, -36.8) * mm});
            skPoint(sketch, "E18.19.16.0", {"position": v(-11.5, -38.54) * mm});
            skArc(sketch, "E18.20.16.0", {"start": v(-13.02, -36.14) * mm, "mid": v(-12.95, -36.88) * mm, "end": v(-12.83, -37.6) * mm});
            skArc(sketch, "E18.24.16.0", {"start": v(-12.83, -37.6) * mm, "mid": v(-12.6, -38.06) * mm, "end": v(-12.18, -38.35) * mm});
            skArc(sketch, "E18.28.16.0", {"start": v(-12.93, -35.51) * mm, "mid": v(-13, -35.82) * mm, "end": v(-13.02, -36.14) * mm});
            skArc(sketch, "E18.32.16.0", {"start": v(-10.06, -37.07) * mm, "mid": v(-9.9, -36.8) * mm, "end": v(-9.78, -36.5) * mm});
            skLineSegment(sketch, "E18.36.16.0", {"start": v(-12.02, -38.4) * mm, "end": v(-12.1, -38.38) * mm});
            skLineSegment(sketch, "E18.39.16.0", {"start": v(-9.78, -36.5) * mm, "end": v(-9.72, -36.26) * mm});
            skLineSegment(sketch, "E18.42.16.0", {"start": v(-12.93, -35.51) * mm, "end": v(-12.84, -35.27) * mm});
            skLineSegment(sketch, "E18.45.16.0", {"start": v(-12.18, -38.35) * mm, "end": v(-12.1, -38.38) * mm});
            skArc(sketch, "E18.3.17.0", {"start": v(-6.52, -36.97) * mm, "mid": v(-6.76, -35.8) * mm, "end": v(-7.74, -35.14) * mm});
            skArc(sketch, "E18.4.17.0", {"start": v(-1.62, -35.95) * mm, "mid": v(-2.74, -36.34) * mm, "end": v(-3.27, -37.4) * mm});
            skArc(sketch, "E18.8.17.0", {"start": v(-5.17, -39.9) * mm, "mid": v(-4.67, -39.82) * mm, "end": v(-4.27, -39.5) * mm});
            skArc(sketch, "E18.12.17.0", {"start": v(-3.47, -38.26) * mm, "mid": v(-3.85, -38.9) * mm, "end": v(-4.27, -39.5) * mm});
            skPoint(sketch, "E18.16.17.0", {"position": v(-5.87, -39.79) * mm});
            skPoint(sketch, "E18.17.17.0", {"position": v(-6.62, -37.52) * mm});
            skPoint(sketch, "E18.18.17.0", {"position": v(-3.32, -37.96) * mm});
            skPoint(sketch, "E18.19.17.0", {"position": v(-4.63, -39.95) * mm});
            skArc(sketch, "E18.20.17.0", {"start": v(-6.55, -37.85) * mm, "mid": v(-6.35, -38.56) * mm, "end": v(-6.1, -39.26) * mm});
            skArc(sketch, "E18.24.17.0", {"start": v(-6.1, -39.26) * mm, "mid": v(-5.8, -39.67) * mm, "end": v(-5.34, -39.88) * mm});
            skArc(sketch, "E18.28.17.0", {"start": v(-6.56, -37.22) * mm, "mid": v(-6.59, -37.54) * mm, "end": v(-6.55, -37.85) * mm});
            skArc(sketch, "E18.32.17.0", {"start": v(-3.47, -38.26) * mm, "mid": v(-3.35, -37.96) * mm, "end": v(-3.3, -37.65) * mm});
            skLineSegment(sketch, "E18.36.17.0", {"start": v(-5.17, -39.9) * mm, "end": v(-5.25, -39.9) * mm});
            skLineSegment(sketch, "E18.39.17.0", {"start": v(-3.3, -37.65) * mm, "end": v(-3.27, -37.4) * mm});
            skLineSegment(sketch, "E18.42.17.0", {"start": v(-6.56, -37.22) * mm, "end": v(-6.52, -36.97) * mm});
            skLineSegment(sketch, "E18.45.17.0", {"start": v(-5.34, -39.88) * mm, "end": v(-5.25, -39.9) * mm});
            skArc(sketch, "E18.3.18.0", {"start": v(0, -37.54) * mm, "mid": v(-0.44, -36.44) * mm, "end": v(-1.52, -35.95) * mm});
            skArc(sketch, "E18.4.18.0", {"start": v(4.65, -35.68) * mm, "mid": v(3.62, -36.26) * mm, "end": v(3.27, -37.4) * mm});
            skArc(sketch, "E18.8.18.0", {"start": v(1.84, -40.2) * mm, "mid": v(2.32, -40.02) * mm, "end": v(2.66, -39.64) * mm});
            skArc(sketch, "E18.12.18.0", {"start": v(3.22, -38.28) * mm, "mid": v(2.97, -38.97) * mm, "end": v(2.66, -39.64) * mm});
            skPoint(sketch, "E18.16.18.0", {"position": v(1.13, -40.2) * mm});
            skPoint(sketch, "E18.17.18.0", {"position": v(0, -38.1) * mm});
            skPoint(sketch, "E18.18.18.0", {"position": v(3.32, -37.96) * mm});
            skPoint(sketch, "E18.19.18.0", {"position": v(2.38, -40.15) * mm});
            skArc(sketch, "E18.20.18.0", {"start": v(0.13, -38.41) * mm, "mid": v(0.44, -39.08) * mm, "end": v(0.8, -39.72) * mm});
            skArc(sketch, "E18.24.18.0", {"start": v(0.8, -39.72) * mm, "mid": v(1.18, -40.07) * mm, "end": v(1.67, -40.2) * mm});
            skArc(sketch, "E18.28.18.0", {"start": v(0, -37.8) * mm, "mid": v(0.03, -38.1) * mm, "end": v(0.13, -38.41) * mm});
            skArc(sketch, "E18.32.18.0", {"start": v(3.22, -38.28) * mm, "mid": v(3.29, -37.97) * mm, "end": v(3.3, -37.65) * mm});
            skLineSegment(sketch, "E18.36.18.0", {"start": v(1.84, -40.2) * mm, "end": v(1.76, -40.2) * mm});
            skLineSegment(sketch, "E18.39.18.0", {"start": v(3.3, -37.65) * mm, "end": v(3.27, -37.4) * mm});
            skLineSegment(sketch, "E18.42.18.0", {"start": v(0, -37.8) * mm, "end": v(0, -37.54) * mm});
            skLineSegment(sketch, "E18.45.18.0", {"start": v(1.67, -40.2) * mm, "end": v(1.76, -40.2) * mm});
            skArc(sketch, "E18.3.19.0", {"start": v(6.52, -36.97) * mm, "mid": v(5.9, -35.96) * mm, "end": v(4.75, -35.67) * mm});
            skArc(sketch, "E18.4.19.0", {"start": v(10.77, -34.33) * mm, "mid": v(9.86, -35.08) * mm, "end": v(9.72, -36.26) * mm});
            skArc(sketch, "E18.8.19.0", {"start": v(8.8, -39.26) * mm, "mid": v(9.23, -39.01) * mm, "end": v(9.5, -38.58) * mm});
            skArc(sketch, "E18.12.19.0", {"start": v(9.82, -37.14) * mm, "mid": v(9.69, -37.86) * mm, "end": v(9.5, -38.58) * mm});
            skPoint(sketch, "E18.16.19.0", {"position": v(8.1, -39.4) * mm});
            skPoint(sketch, "E18.17.19.0", {"position": v(6.62, -37.52) * mm});
            skPoint(sketch, "E18.18.19.0", {"position": v(9.86, -36.8) * mm});
            skPoint(sketch, "E18.19.19.0", {"position": v(9.32, -39.12) * mm});
            skArc(sketch, "E18.20.19.0", {"start": v(6.8, -37.8) * mm, "mid": v(7.22, -38.41) * mm, "end": v(7.7, -38.98) * mm});
            skArc(sketch, "E18.24.19.0", {"start": v(7.7, -38.98) * mm, "mid": v(8.12, -39.26) * mm, "end": v(8.63, -39.3) * mm});
            skArc(sketch, "E18.28.19.0", {"start": v(6.56, -37.22) * mm, "mid": v(6.65, -37.52) * mm, "end": v(6.8, -37.8) * mm});
            skArc(sketch, "E18.32.19.0", {"start": v(9.82, -37.14) * mm, "mid": v(9.83, -36.82) * mm, "end": v(9.78, -36.5) * mm});
            skLineSegment(sketch, "E18.36.19.0", {"start": v(8.8, -39.26) * mm, "end": v(8.7, -39.29) * mm});
            skLineSegment(sketch, "E18.39.19.0", {"start": v(9.78, -36.5) * mm, "end": v(9.72, -36.26) * mm});
            skLineSegment(sketch, "E18.42.19.0", {"start": v(6.56, -37.22) * mm, "end": v(6.52, -36.97) * mm});
            skLineSegment(sketch, "E18.45.19.0", {"start": v(8.63, -39.3) * mm, "end": v(8.7, -39.29) * mm});
            skArc(sketch, "E18.3.20.0", {"start": v(12.84, -35.27) * mm, "mid": v(12.05, -34.4) * mm, "end": v(10.87, -34.3) * mm});
            skArc(sketch, "E18.4.20.0", {"start": v(16.57, -31.94) * mm, "mid": v(15.8, -32.84) * mm, "end": v(15.86, -34.02) * mm});
            skArc(sketch, "E18.8.20.0", {"start": v(15.48, -37.14) * mm, "mid": v(15.87, -36.82) * mm, "end": v(16.05, -36.34) * mm});
            skArc(sketch, "E18.12.20.0", {"start": v(16.12, -34.87) * mm, "mid": v(16.12, -35.6) * mm, "end": v(16.05, -36.34) * mm});
            skPoint(sketch, "E18.16.20.0", {"position": v(14.8, -37.4) * mm});
            skPoint(sketch, "E18.17.20.0", {"position": v(13.03, -35.8) * mm});
            skPoint(sketch, "E18.18.20.0", {"position": v(16.1, -34.53) * mm});
            skPoint(sketch, "E18.19.20.0", {"position": v(15.97, -36.91) * mm});
            skArc(sketch, "E18.20.20.0", {"start": v(13.26, -36.05) * mm, "mid": v(13.78, -36.57) * mm, "end": v(14.35, -37.05) * mm});
            skArc(sketch, "E18.24.20.0", {"start": v(14.35, -37.05) * mm, "mid": v(14.81, -37.25) * mm, "end": v(15.32, -37.2) * mm});
            skArc(sketch, "E18.28.20.0", {"start": v(12.93, -35.51) * mm, "mid": v(13.06, -35.8) * mm, "end": v(13.26, -36.05) * mm});
            skArc(sketch, "E18.32.20.0", {"start": v(16.12, -34.87) * mm, "mid": v(16.08, -34.55) * mm, "end": v(15.97, -34.25) * mm});
            skLineSegment(sketch, "E18.36.20.0", {"start": v(15.48, -37.14) * mm, "end": v(15.4, -37.18) * mm});
            skLineSegment(sketch, "E18.39.20.0", {"start": v(15.97, -34.25) * mm, "end": v(15.86, -34.02) * mm});
            skLineSegment(sketch, "E18.42.20.0", {"start": v(12.93, -35.51) * mm, "end": v(12.84, -35.27) * mm});
            skLineSegment(sketch, "E18.45.20.0", {"start": v(15.32, -37.2) * mm, "end": v(15.4, -37.18) * mm});
            skArc(sketch, "E18.3.21.0", {"start": v(18.77, -32.5) * mm, "mid": v(17.84, -31.78) * mm, "end": v(16.66, -31.9) * mm});
            skArc(sketch, "E18.4.21.0", {"start": v(21.87, -28.58) * mm, "mid": v(21.26, -29.6) * mm, "end": v(21.53, -30.75) * mm});
            skArc(sketch, "E18.8.21.0", {"start": v(21.69, -33.89) * mm, "mid": v(22.02, -33.5) * mm, "end": v(22.12, -33) * mm});
            skArc(sketch, "E18.12.21.0", {"start": v(21.93, -31.54) * mm, "mid": v(22.05, -32.27) * mm, "end": v(22.12, -33) * mm});
            skPoint(sketch, "E18.16.21.0", {"position": v(21.08, -34.25) * mm});
            skPoint(sketch, "E18.17.21.0", {"position": v(19.05, -33) * mm});
            skPoint(sketch, "E18.18.21.0", {"position": v(21.85, -31.2) * mm});
            skPoint(sketch, "E18.19.21.0", {"position": v(22.13, -33.58) * mm});
            skArc(sketch, "E18.20.21.0", {"start": v(19.32, -33.2) * mm, "mid": v(19.92, -33.62) * mm, "end": v(20.56, -34) * mm});
            skArc(sketch, "E18.24.21.0", {"start": v(20.56, -34) * mm, "mid": v(21.06, -34.12) * mm, "end": v(21.55, -33.98) * mm});
            skArc(sketch, "E18.28.21.0", {"start": v(18.9, -32.73) * mm, "mid": v(19.08, -32.99) * mm, "end": v(19.32, -33.2) * mm});
            skArc(sketch, "E18.32.21.0", {"start": v(21.93, -31.54) * mm, "mid": v(21.83, -31.24) * mm, "end": v(21.68, -30.96) * mm});
            skLineSegment(sketch, "E18.36.21.0", {"start": v(21.69, -33.89) * mm, "end": v(21.62, -33.94) * mm});
            skLineSegment(sketch, "E18.39.21.0", {"start": v(21.68, -30.96) * mm, "end": v(21.53, -30.75) * mm});
            skLineSegment(sketch, "E18.42.21.0", {"start": v(18.9, -32.73) * mm, "end": v(18.77, -32.5) * mm});
            skLineSegment(sketch, "E18.45.21.0", {"start": v(21.55, -33.98) * mm, "end": v(21.62, -33.94) * mm});
            skArc(sketch, "E18.3.22.0", {"start": v(24.13, -28.76) * mm, "mid": v(23.08, -28.2) * mm, "end": v(21.94, -28.52) * mm});
            skArc(sketch, "E18.4.22.0", {"start": v(26.5, -24.35) * mm, "mid": v(26.08, -25.45) * mm, "end": v(26.54, -26.54) * mm});
            skArc(sketch, "E18.8.22.0", {"start": v(27.24, -29.6) * mm, "mid": v(27.5, -29.17) * mm, "end": v(27.52, -28.66) * mm});
            skArc(sketch, "E18.12.22.0", {"start": v(27.07, -27.25) * mm, "mid": v(27.32, -27.95) * mm, "end": v(27.52, -28.66) * mm});
            skPoint(sketch, "E18.16.22.0", {"position": v(26.7, -30.07) * mm});
            skPoint(sketch, "E18.17.22.0", {"position": v(24.5, -29.19) * mm});
            skPoint(sketch, "E18.18.22.0", {"position": v(26.94, -26.94) * mm});
            skPoint(sketch, "E18.19.22.0", {"position": v(27.63, -29.22) * mm});
            skArc(sketch, "E18.20.22.0", {"start": v(24.79, -29.34) * mm, "mid": v(25.46, -29.65) * mm, "end": v(26.15, -29.9) * mm});
            skArc(sketch, "E18.24.22.0", {"start": v(26.15, -29.9) * mm, "mid": v(26.66, -29.94) * mm, "end": v(27.12, -29.72) * mm});
            skArc(sketch, "E18.28.22.0", {"start": v(24.3, -28.95) * mm, "mid": v(24.52, -29.17) * mm, "end": v(24.79, -29.34) * mm});
            skArc(sketch, "E18.32.22.0", {"start": v(27.07, -27.25) * mm, "mid": v(26.92, -26.97) * mm, "end": v(26.72, -26.72) * mm});
            skLineSegment(sketch, "E18.36.22.0", {"start": v(27.24, -29.6) * mm, "end": v(27.19, -29.67) * mm});
            skLineSegment(sketch, "E18.39.22.0", {"start": v(26.72, -26.72) * mm, "end": v(26.54, -26.54) * mm});
            skLineSegment(sketch, "E18.42.22.0", {"start": v(24.3, -28.95) * mm, "end": v(24.13, -28.76) * mm});
            skLineSegment(sketch, "E18.45.22.0", {"start": v(27.12, -29.72) * mm, "end": v(27.19, -29.67) * mm});
            skArc(sketch, "E18.3.23.0", {"start": v(28.76, -24.13) * mm, "mid": v(27.63, -23.76) * mm, "end": v(26.56, -24.27) * mm});
            skArc(sketch, "E18.4.23.0", {"start": v(30.32, -19.38) * mm, "mid": v(30.1, -20.54) * mm, "end": v(30.75, -21.53) * mm});
            skArc(sketch, "E18.8.23.0", {"start": v(31.97, -24.43) * mm, "mid": v(32.15, -23.95) * mm, "end": v(32.07, -23.45) * mm});
            skArc(sketch, "E18.12.23.0", {"start": v(31.4, -22.14) * mm, "mid": v(31.76, -22.78) * mm, "end": v(32.07, -23.45) * mm});
            skPoint(sketch, "E18.16.23.0", {"position": v(31.52, -24.98) * mm});
            skPoint(sketch, "E18.17.23.0", {"position": v(29.19, -24.5) * mm});
            skPoint(sketch, "E18.18.23.0", {"position": v(31.2, -21.85) * mm});
            skPoint(sketch, "E18.19.23.0", {"position": v(32.28, -23.98) * mm});
            skArc(sketch, "E18.20.23.0", {"start": v(29.5, -24.6) * mm, "mid": v(30.22, -24.78) * mm, "end": v(30.95, -24.91) * mm});
            skArc(sketch, "E18.24.23.0", {"start": v(30.95, -24.91) * mm, "mid": v(31.46, -24.86) * mm, "end": v(31.87, -24.56) * mm});
            skArc(sketch, "E18.28.23.0", {"start": v(28.95, -24.3) * mm, "mid": v(29.21, -24.47) * mm, "end": v(29.5, -24.6) * mm});
            skArc(sketch, "E18.32.23.0", {"start": v(31.4, -22.14) * mm, "mid": v(31.2, -21.88) * mm, "end": v(30.96, -21.68) * mm});
            skLineSegment(sketch, "E18.36.23.0", {"start": v(31.97, -24.43) * mm, "end": v(31.92, -24.5) * mm});
            skLineSegment(sketch, "E18.39.23.0", {"start": v(30.96, -21.68) * mm, "end": v(30.75, -21.53) * mm});
            skLineSegment(sketch, "E18.42.23.0", {"start": v(28.95, -24.3) * mm, "end": v(28.76, -24.13) * mm});
            skLineSegment(sketch, "E18.45.23.0", {"start": v(31.87, -24.56) * mm, "end": v(31.92, -24.5) * mm});
            skArc(sketch, "E18.3.24.0", {"start": v(32.5, -18.77) * mm, "mid": v(31.34, -18.6) * mm, "end": v(30.37, -19.3) * mm});
            skArc(sketch, "E18.4.24.0", {"start": v(33.23, -13.82) * mm, "mid": v(33.21, -15) * mm, "end": v(34.02, -15.86) * mm});
            skArc(sketch, "E18.8.24.0", {"start": v(35.73, -18.5) * mm, "mid": v(35.82, -18) * mm, "end": v(35.66, -17.52) * mm});
            skArc(sketch, "E18.12.24.0", {"start": v(34.76, -16.35) * mm, "mid": v(35.23, -16.92) * mm, "end": v(35.66, -17.52) * mm});
            skPoint(sketch, "E18.16.24.0", {"position": v(35.38, -19.12) * mm});
            skPoint(sketch, "E18.17.24.0", {"position": v(33, -19.05) * mm});
            skPoint(sketch, "E18.18.24.0", {"position": v(34.53, -16.1) * mm});
            skPoint(sketch, "E18.19.24.0", {"position": v(35.96, -18.01) * mm});
            skArc(sketch, "E18.20.24.0", {"start": v(33.33, -19.1) * mm, "mid": v(34.07, -19.16) * mm, "end": v(34.8, -19.16) * mm});
            skArc(sketch, "E18.24.24.0", {"start": v(34.8, -19.16) * mm, "mid": v(35.3, -19.02) * mm, "end": v(35.65, -18.65) * mm});
            skArc(sketch, "E18.28.24.0", {"start": v(32.73, -18.9) * mm, "mid": v(33.02, -19.03) * mm, "end": v(33.33, -19.1) * mm});
            skArc(sketch, "E18.32.24.0", {"start": v(34.76, -16.35) * mm, "mid": v(34.52, -16.13) * mm, "end": v(34.25, -15.97) * mm});
            skLineSegment(sketch, "E18.36.24.0", {"start": v(35.73, -18.5) * mm, "end": v(35.7, -18.58) * mm});
            skLineSegment(sketch, "E18.39.24.0", {"start": v(34.25, -15.97) * mm, "end": v(34.02, -15.86) * mm});
            skLineSegment(sketch, "E18.42.24.0", {"start": v(32.73, -18.9) * mm, "end": v(32.5, -18.77) * mm});
            skLineSegment(sketch, "E18.45.24.0", {"start": v(35.65, -18.65) * mm, "end": v(35.7, -18.58) * mm});
            skArc(sketch, "E18.3.25.0", {"start": v(35.27, -12.84) * mm, "mid": v(34.1, -12.88) * mm, "end": v(33.26, -13.72) * mm});
            skArc(sketch, "E18.4.25.0", {"start": v(35.12, -7.84) * mm, "mid": v(35.31, -9) * mm, "end": v(36.26, -9.72) * mm});
            skArc(sketch, "E18.8.25.0", {"start": v(38.4, -12.02) * mm, "mid": v(38.4, -11.5) * mm, "end": v(38.16, -11.06) * mm});
            skArc(sketch, "E18.12.25.0", {"start": v(37.07, -10.06) * mm, "mid": v(37.64, -10.54) * mm, "end": v(38.16, -11.06) * mm});
            skPoint(sketch, "E18.16.25.0", {"position": v(38.16, -12.69) * mm});
            skPoint(sketch, "E18.17.25.0", {"position": v(35.8, -13.03) * mm});
            skPoint(sketch, "E18.18.25.0", {"position": v(36.8, -9.86) * mm});
            skPoint(sketch, "E18.19.25.0", {"position": v(38.54, -11.5) * mm});
            skArc(sketch, "E18.20.25.0", {"start": v(36.14, -13.02) * mm, "mid": v(36.88, -12.95) * mm, "end": v(37.6, -12.83) * mm});
            skArc(sketch, "E18.24.25.0", {"start": v(37.6, -12.83) * mm, "mid": v(38.06, -12.6) * mm, "end": v(38.35, -12.18) * mm});
            skArc(sketch, "E18.28.25.0", {"start": v(35.51, -12.93) * mm, "mid": v(35.82, -13) * mm, "end": v(36.14, -13.02) * mm});
            skArc(sketch, "E18.32.25.0", {"start": v(37.07, -10.06) * mm, "mid": v(36.8, -9.9) * mm, "end": v(36.5, -9.78) * mm});
            skLineSegment(sketch, "E18.36.25.0", {"start": v(38.4, -12.02) * mm, "end": v(38.38, -12.1) * mm});
            skLineSegment(sketch, "E18.39.25.0", {"start": v(36.5, -9.78) * mm, "end": v(36.26, -9.72) * mm});
            skLineSegment(sketch, "E18.42.25.0", {"start": v(35.51, -12.93) * mm, "end": v(35.27, -12.84) * mm});
            skLineSegment(sketch, "E18.45.25.0", {"start": v(38.35, -12.18) * mm, "end": v(38.38, -12.1) * mm});
            skArc(sketch, "E18.3.26.0", {"start": v(36.97, -6.52) * mm, "mid": v(35.8, -6.76) * mm, "end": v(35.14, -7.74) * mm});
            skArc(sketch, "E18.4.26.0", {"start": v(35.95, -1.62) * mm, "mid": v(36.34, -2.74) * mm, "end": v(37.4, -3.27) * mm});
            skArc(sketch, "E18.8.26.0", {"start": v(39.9, -5.17) * mm, "mid": v(39.82, -4.67) * mm, "end": v(39.5, -4.27) * mm});
            skArc(sketch, "E18.12.26.0", {"start": v(38.26, -3.47) * mm, "mid": v(38.9, -3.85) * mm, "end": v(39.5, -4.27) * mm});
            skPoint(sketch, "E18.16.26.0", {"position": v(39.79, -5.87) * mm});
            skPoint(sketch, "E18.17.26.0", {"position": v(37.52, -6.62) * mm});
            skPoint(sketch, "E18.18.26.0", {"position": v(37.96, -3.32) * mm});
            skPoint(sketch, "E18.19.26.0", {"position": v(39.95, -4.63) * mm});
            skArc(sketch, "E18.20.26.0", {"start": v(37.85, -6.55) * mm, "mid": v(38.56, -6.35) * mm, "end": v(39.26, -6.1) * mm});
            skArc(sketch, "E18.24.26.0", {"start": v(39.26, -6.1) * mm, "mid": v(39.67, -5.8) * mm, "end": v(39.88, -5.34) * mm});
            skArc(sketch, "E18.28.26.0", {"start": v(37.22, -6.56) * mm, "mid": v(37.54, -6.59) * mm, "end": v(37.85, -6.55) * mm});
            skArc(sketch, "E18.32.26.0", {"start": v(38.26, -3.47) * mm, "mid": v(37.96, -3.35) * mm, "end": v(37.65, -3.3) * mm});
            skLineSegment(sketch, "E18.36.26.0", {"start": v(39.9, -5.17) * mm, "end": v(39.9, -5.25) * mm});
            skLineSegment(sketch, "E18.39.26.0", {"start": v(37.65, -3.3) * mm, "end": v(37.4, -3.27) * mm});
            skLineSegment(sketch, "E18.42.26.0", {"start": v(37.22, -6.56) * mm, "end": v(36.97, -6.52) * mm});
            skLineSegment(sketch, "E18.45.26.0", {"start": v(39.88, -5.34) * mm, "end": v(39.9, -5.25) * mm});
            skArc(sketch, "E18.3.27.0", {"start": v(37.54, 0) * mm, "mid": v(36.44, -0.44) * mm, "end": v(35.95, -1.52) * mm});
            skArc(sketch, "E18.4.27.0", {"start": v(35.68, 4.65) * mm, "mid": v(36.26, 3.62) * mm, "end": v(37.4, 3.27) * mm});
            skArc(sketch, "E18.8.27.0", {"start": v(40.2, 1.84) * mm, "mid": v(40.02, 2.32) * mm, "end": v(39.64, 2.66) * mm});
            skArc(sketch, "E18.12.27.0", {"start": v(38.28, 3.22) * mm, "mid": v(38.97, 2.97) * mm, "end": v(39.64, 2.66) * mm});
            skPoint(sketch, "E18.16.27.0", {"position": v(40.2, 1.13) * mm});
            skPoint(sketch, "E18.17.27.0", {"position": v(38.1, 0) * mm});
            skPoint(sketch, "E18.18.27.0", {"position": v(37.96, 3.32) * mm});
            skPoint(sketch, "E18.19.27.0", {"position": v(40.15, 2.38) * mm});
            skArc(sketch, "E18.20.27.0", {"start": v(38.41, 0.13) * mm, "mid": v(39.08, 0.44) * mm, "end": v(39.72, 0.8) * mm});
            skArc(sketch, "E18.24.27.0", {"start": v(39.72, 0.8) * mm, "mid": v(40.07, 1.18) * mm, "end": v(40.2, 1.67) * mm});
            skArc(sketch, "E18.28.27.0", {"start": v(37.8, 0) * mm, "mid": v(38.1, 0.03) * mm, "end": v(38.41, 0.13) * mm});
            skArc(sketch, "E18.32.27.0", {"start": v(38.28, 3.22) * mm, "mid": v(37.97, 3.29) * mm, "end": v(37.65, 3.3) * mm});
            skLineSegment(sketch, "E18.36.27.0", {"start": v(40.2, 1.84) * mm, "end": v(40.2, 1.76) * mm});
            skLineSegment(sketch, "E18.39.27.0", {"start": v(37.65, 3.3) * mm, "end": v(37.4, 3.27) * mm});
            skLineSegment(sketch, "E18.42.27.0", {"start": v(37.8, 0) * mm, "end": v(37.54, 0) * mm});
            skLineSegment(sketch, "E18.45.27.0", {"start": v(40.2, 1.67) * mm, "end": v(40.2, 1.76) * mm});
            skArc(sketch, "E18.3.28.0", {"start": v(36.97, 6.52) * mm, "mid": v(35.96, 5.9) * mm, "end": v(35.67, 4.75) * mm});
            skArc(sketch, "E18.4.28.0", {"start": v(34.33, 10.77) * mm, "mid": v(35.08, 9.86) * mm, "end": v(36.26, 9.72) * mm});
            skArc(sketch, "E18.8.28.0", {"start": v(39.26, 8.8) * mm, "mid": v(39.01, 9.23) * mm, "end": v(38.58, 9.5) * mm});
            skArc(sketch, "E18.12.28.0", {"start": v(37.14, 9.82) * mm, "mid": v(37.86, 9.69) * mm, "end": v(38.58, 9.5) * mm});
            skPoint(sketch, "E18.16.28.0", {"position": v(39.4, 8.1) * mm});
            skPoint(sketch, "E18.17.28.0", {"position": v(37.52, 6.62) * mm});
            skPoint(sketch, "E18.18.28.0", {"position": v(36.8, 9.86) * mm});
            skPoint(sketch, "E18.19.28.0", {"position": v(39.12, 9.32) * mm});
            skArc(sketch, "E18.20.28.0", {"start": v(37.8, 6.8) * mm, "mid": v(38.41, 7.22) * mm, "end": v(38.98, 7.7) * mm});
            skArc(sketch, "E18.24.28.0", {"start": v(38.98, 7.7) * mm, "mid": v(39.26, 8.12) * mm, "end": v(39.3, 8.63) * mm});
            skArc(sketch, "E18.28.28.0", {"start": v(37.22, 6.56) * mm, "mid": v(37.52, 6.65) * mm, "end": v(37.8, 6.8) * mm});
            skArc(sketch, "E18.32.28.0", {"start": v(37.14, 9.82) * mm, "mid": v(36.82, 9.83) * mm, "end": v(36.5, 9.78) * mm});
            skLineSegment(sketch, "E18.36.28.0", {"start": v(39.26, 8.8) * mm, "end": v(39.29, 8.7) * mm});
            skLineSegment(sketch, "E18.39.28.0", {"start": v(36.5, 9.78) * mm, "end": v(36.26, 9.72) * mm});
            skLineSegment(sketch, "E18.42.28.0", {"start": v(37.22, 6.56) * mm, "end": v(36.97, 6.52) * mm});
            skLineSegment(sketch, "E18.45.28.0", {"start": v(39.3, 8.63) * mm, "end": v(39.29, 8.7) * mm});
            skArc(sketch, "E18.3.29.0", {"start": v(35.27, 12.84) * mm, "mid": v(34.4, 12.05) * mm, "end": v(34.3, 10.87) * mm});
            skArc(sketch, "E18.4.29.0", {"start": v(31.94, 16.57) * mm, "mid": v(32.84, 15.8) * mm, "end": v(34.02, 15.86) * mm});
            skArc(sketch, "E18.8.29.0", {"start": v(37.14, 15.48) * mm, "mid": v(36.82, 15.87) * mm, "end": v(36.34, 16.05) * mm});
            skArc(sketch, "E18.12.29.0", {"start": v(34.87, 16.12) * mm, "mid": v(35.6, 16.12) * mm, "end": v(36.34, 16.05) * mm});
            skPoint(sketch, "E18.16.29.0", {"position": v(37.4, 14.8) * mm});
            skPoint(sketch, "E18.17.29.0", {"position": v(35.8, 13.03) * mm});
            skPoint(sketch, "E18.18.29.0", {"position": v(34.53, 16.1) * mm});
            skPoint(sketch, "E18.19.29.0", {"position": v(36.91, 15.97) * mm});
            skArc(sketch, "E18.20.29.0", {"start": v(36.05, 13.26) * mm, "mid": v(36.57, 13.78) * mm, "end": v(37.05, 14.35) * mm});
            skArc(sketch, "E18.24.29.0", {"start": v(37.05, 14.35) * mm, "mid": v(37.25, 14.81) * mm, "end": v(37.2, 15.32) * mm});
            skArc(sketch, "E18.28.29.0", {"start": v(35.51, 12.93) * mm, "mid": v(35.8, 13.06) * mm, "end": v(36.05, 13.26) * mm});
            skArc(sketch, "E18.32.29.0", {"start": v(34.87, 16.12) * mm, "mid": v(34.55, 16.08) * mm, "end": v(34.25, 15.97) * mm});
            skLineSegment(sketch, "E18.36.29.0", {"start": v(37.14, 15.48) * mm, "end": v(37.18, 15.4) * mm});
            skLineSegment(sketch, "E18.39.29.0", {"start": v(34.25, 15.97) * mm, "end": v(34.02, 15.86) * mm});
            skLineSegment(sketch, "E18.42.29.0", {"start": v(35.51, 12.93) * mm, "end": v(35.27, 12.84) * mm});
            skLineSegment(sketch, "E18.45.29.0", {"start": v(37.2, 15.32) * mm, "end": v(37.18, 15.4) * mm});
            skArc(sketch, "E18.3.30.0", {"start": v(32.5, 18.77) * mm, "mid": v(31.78, 17.84) * mm, "end": v(31.9, 16.66) * mm});
            skArc(sketch, "E18.4.30.0", {"start": v(28.58, 21.87) * mm, "mid": v(29.6, 21.26) * mm, "end": v(30.75, 21.53) * mm});
            skArc(sketch, "E18.8.30.0", {"start": v(33.89, 21.69) * mm, "mid": v(33.5, 22.02) * mm, "end": v(33, 22.12) * mm});
            skArc(sketch, "E18.12.30.0", {"start": v(31.54, 21.93) * mm, "mid": v(32.27, 22.05) * mm, "end": v(33, 22.12) * mm});
            skPoint(sketch, "E18.16.30.0", {"position": v(34.25, 21.08) * mm});
            skPoint(sketch, "E18.17.30.0", {"position": v(33, 19.05) * mm});
            skPoint(sketch, "E18.18.30.0", {"position": v(31.2, 21.85) * mm});
            skPoint(sketch, "E18.19.30.0", {"position": v(33.58, 22.13) * mm});
            skArc(sketch, "E18.20.30.0", {"start": v(33.2, 19.32) * mm, "mid": v(33.62, 19.92) * mm, "end": v(34, 20.56) * mm});
            skArc(sketch, "E18.24.30.0", {"start": v(34, 20.56) * mm, "mid": v(34.12, 21.06) * mm, "end": v(33.98, 21.55) * mm});
            skArc(sketch, "E18.28.30.0", {"start": v(32.73, 18.9) * mm, "mid": v(32.99, 19.08) * mm, "end": v(33.2, 19.32) * mm});
            skArc(sketch, "E18.32.30.0", {"start": v(31.54, 21.93) * mm, "mid": v(31.24, 21.83) * mm, "end": v(30.96, 21.68) * mm});
            skLineSegment(sketch, "E18.36.30.0", {"start": v(33.89, 21.69) * mm, "end": v(33.94, 21.62) * mm});
            skLineSegment(sketch, "E18.39.30.0", {"start": v(30.96, 21.68) * mm, "end": v(30.75, 21.53) * mm});
            skLineSegment(sketch, "E18.42.30.0", {"start": v(32.73, 18.9) * mm, "end": v(32.5, 18.77) * mm});
            skLineSegment(sketch, "E18.45.30.0", {"start": v(33.98, 21.55) * mm, "end": v(33.94, 21.62) * mm});
            skArc(sketch, "E18.3.31.0", {"start": v(28.76, 24.13) * mm, "mid": v(28.2, 23.08) * mm, "end": v(28.52, 21.94) * mm});
            skArc(sketch, "E18.4.31.0", {"start": v(24.35, 26.5) * mm, "mid": v(25.45, 26.08) * mm, "end": v(26.54, 26.54) * mm});
            skArc(sketch, "E18.8.31.0", {"start": v(29.6, 27.24) * mm, "mid": v(29.17, 27.5) * mm, "end": v(28.66, 27.52) * mm});
            skArc(sketch, "E18.12.31.0", {"start": v(27.25, 27.07) * mm, "mid": v(27.95, 27.32) * mm, "end": v(28.66, 27.52) * mm});
            skPoint(sketch, "E18.16.31.0", {"position": v(30.07, 26.7) * mm});
            skPoint(sketch, "E18.17.31.0", {"position": v(29.19, 24.5) * mm});
            skPoint(sketch, "E18.18.31.0", {"position": v(26.94, 26.94) * mm});
            skPoint(sketch, "E18.19.31.0", {"position": v(29.22, 27.63) * mm});
            skArc(sketch, "E18.20.31.0", {"start": v(29.34, 24.79) * mm, "mid": v(29.65, 25.46) * mm, "end": v(29.9, 26.15) * mm});
            skArc(sketch, "E18.24.31.0", {"start": v(29.9, 26.15) * mm, "mid": v(29.94, 26.66) * mm, "end": v(29.72, 27.12) * mm});
            skArc(sketch, "E18.28.31.0", {"start": v(28.95, 24.3) * mm, "mid": v(29.17, 24.52) * mm, "end": v(29.34, 24.79) * mm});
            skArc(sketch, "E18.32.31.0", {"start": v(27.25, 27.07) * mm, "mid": v(26.97, 26.92) * mm, "end": v(26.72, 26.72) * mm});
            skLineSegment(sketch, "E18.36.31.0", {"start": v(29.6, 27.24) * mm, "end": v(29.67, 27.19) * mm});
            skLineSegment(sketch, "E18.39.31.0", {"start": v(26.72, 26.72) * mm, "end": v(26.54, 26.54) * mm});
            skLineSegment(sketch, "E18.42.31.0", {"start": v(28.95, 24.3) * mm, "end": v(28.76, 24.13) * mm});
            skLineSegment(sketch, "E18.45.31.0", {"start": v(29.72, 27.12) * mm, "end": v(29.67, 27.19) * mm});
            skArc(sketch, "E18.3.32.0", {"start": v(24.13, 28.76) * mm, "mid": v(23.76, 27.63) * mm, "end": v(24.27, 26.56) * mm});
            skArc(sketch, "E18.4.32.0", {"start": v(19.38, 30.32) * mm, "mid": v(20.54, 30.1) * mm, "end": v(21.53, 30.75) * mm});
            skArc(sketch, "E18.8.32.0", {"start": v(24.43, 31.97) * mm, "mid": v(23.95, 32.15) * mm, "end": v(23.45, 32.07) * mm});
            skArc(sketch, "E18.12.32.0", {"start": v(22.14, 31.4) * mm, "mid": v(22.78, 31.76) * mm, "end": v(23.45, 32.07) * mm});
            skPoint(sketch, "E18.16.32.0", {"position": v(24.98, 31.52) * mm});
            skPoint(sketch, "E18.17.32.0", {"position": v(24.5, 29.19) * mm});
            skPoint(sketch, "E18.18.32.0", {"position": v(21.85, 31.2) * mm});
            skPoint(sketch, "E18.19.32.0", {"position": v(23.98, 32.28) * mm});
            skArc(sketch, "E18.20.32.0", {"start": v(24.6, 29.5) * mm, "mid": v(24.78, 30.22) * mm, "end": v(24.91, 30.95) * mm});
            skArc(sketch, "E18.24.32.0", {"start": v(24.91, 30.95) * mm, "mid": v(24.86, 31.46) * mm, "end": v(24.56, 31.87) * mm});
            skArc(sketch, "E18.28.32.0", {"start": v(24.3, 28.95) * mm, "mid": v(24.47, 29.21) * mm, "end": v(24.6, 29.5) * mm});
            skArc(sketch, "E18.32.32.0", {"start": v(22.14, 31.4) * mm, "mid": v(21.88, 31.2) * mm, "end": v(21.68, 30.96) * mm});
            skLineSegment(sketch, "E18.36.32.0", {"start": v(24.43, 31.97) * mm, "end": v(24.5, 31.92) * mm});
            skLineSegment(sketch, "E18.39.32.0", {"start": v(21.68, 30.96) * mm, "end": v(21.53, 30.75) * mm});
            skLineSegment(sketch, "E18.42.32.0", {"start": v(24.3, 28.95) * mm, "end": v(24.13, 28.76) * mm});
            skLineSegment(sketch, "E18.45.32.0", {"start": v(24.56, 31.87) * mm, "end": v(24.5, 31.92) * mm});
            skArc(sketch, "E18.3.33.0", {"start": v(18.77, 32.5) * mm, "mid": v(18.6, 31.34) * mm, "end": v(19.3, 30.37) * mm});
            skArc(sketch, "E18.4.33.0", {"start": v(13.82, 33.23) * mm, "mid": v(15, 33.21) * mm, "end": v(15.86, 34.02) * mm});
            skArc(sketch, "E18.8.33.0", {"start": v(18.5, 35.73) * mm, "mid": v(18, 35.82) * mm, "end": v(17.52, 35.66) * mm});
            skArc(sketch, "E18.12.33.0", {"start": v(16.35, 34.76) * mm, "mid": v(16.92, 35.23) * mm, "end": v(17.52, 35.66) * mm});
            skPoint(sketch, "E18.16.33.0", {"position": v(19.12, 35.38) * mm});
            skPoint(sketch, "E18.17.33.0", {"position": v(19.05, 33) * mm});
            skPoint(sketch, "E18.18.33.0", {"position": v(16.1, 34.53) * mm});
            skPoint(sketch, "E18.19.33.0", {"position": v(18.01, 35.96) * mm});
            skArc(sketch, "E18.20.33.0", {"start": v(19.1, 33.33) * mm, "mid": v(19.16, 34.07) * mm, "end": v(19.16, 34.8) * mm});
            skArc(sketch, "E18.24.33.0", {"start": v(19.16, 34.8) * mm, "mid": v(19.02, 35.3) * mm, "end": v(18.65, 35.65) * mm});
            skArc(sketch, "E18.28.33.0", {"start": v(18.9, 32.73) * mm, "mid": v(19.03, 33.02) * mm, "end": v(19.1, 33.33) * mm});
            skArc(sketch, "E18.32.33.0", {"start": v(16.35, 34.76) * mm, "mid": v(16.13, 34.52) * mm, "end": v(15.97, 34.25) * mm});
            skLineSegment(sketch, "E18.36.33.0", {"start": v(18.5, 35.73) * mm, "end": v(18.58, 35.7) * mm});
            skLineSegment(sketch, "E18.39.33.0", {"start": v(15.97, 34.25) * mm, "end": v(15.86, 34.02) * mm});
            skLineSegment(sketch, "E18.42.33.0", {"start": v(18.9, 32.73) * mm, "end": v(18.77, 32.5) * mm});
            skLineSegment(sketch, "E18.45.33.0", {"start": v(18.65, 35.65) * mm, "end": v(18.58, 35.7) * mm});
            skArc(sketch, "E18.3.34.0", {"start": v(12.84, 35.27) * mm, "mid": v(12.88, 34.1) * mm, "end": v(13.72, 33.26) * mm});
            skArc(sketch, "E18.4.34.0", {"start": v(7.84, 35.12) * mm, "mid": v(9, 35.31) * mm, "end": v(9.72, 36.26) * mm});
            skArc(sketch, "E18.8.34.0", {"start": v(12.02, 38.4) * mm, "mid": v(11.5, 38.4) * mm, "end": v(11.06, 38.16) * mm});
            skArc(sketch, "E18.12.34.0", {"start": v(10.06, 37.07) * mm, "mid": v(10.54, 37.64) * mm, "end": v(11.06, 38.16) * mm});
            skPoint(sketch, "E18.16.34.0", {"position": v(12.69, 38.16) * mm});
            skPoint(sketch, "E18.17.34.0", {"position": v(13.03, 35.8) * mm});
            skPoint(sketch, "E18.18.34.0", {"position": v(9.86, 36.8) * mm});
            skPoint(sketch, "E18.19.34.0", {"position": v(11.5, 38.54) * mm});
            skArc(sketch, "E18.20.34.0", {"start": v(13.02, 36.14) * mm, "mid": v(12.95, 36.88) * mm, "end": v(12.83, 37.6) * mm});
            skArc(sketch, "E18.24.34.0", {"start": v(12.83, 37.6) * mm, "mid": v(12.6, 38.06) * mm, "end": v(12.18, 38.35) * mm});
            skArc(sketch, "E18.28.34.0", {"start": v(12.93, 35.51) * mm, "mid": v(13, 35.82) * mm, "end": v(13.02, 36.14) * mm});
            skArc(sketch, "E18.32.34.0", {"start": v(10.06, 37.07) * mm, "mid": v(9.9, 36.8) * mm, "end": v(9.78, 36.5) * mm});
            skLineSegment(sketch, "E18.36.34.0", {"start": v(12.02, 38.4) * mm, "end": v(12.1, 38.38) * mm});
            skLineSegment(sketch, "E18.39.34.0", {"start": v(9.78, 36.5) * mm, "end": v(9.72, 36.26) * mm});
            skLineSegment(sketch, "E18.42.34.0", {"start": v(12.93, 35.51) * mm, "end": v(12.84, 35.27) * mm});
            skLineSegment(sketch, "E18.45.34.0", {"start": v(12.18, 38.35) * mm, "end": v(12.1, 38.38) * mm});
            skArc(sketch, "E18.3.35.0", {"start": v(6.52, 36.97) * mm, "mid": v(6.76, 35.8) * mm, "end": v(7.74, 35.14) * mm});
            skArc(sketch, "E18.4.35.0", {"start": v(1.62, 35.95) * mm, "mid": v(2.74, 36.34) * mm, "end": v(3.27, 37.4) * mm});
            skArc(sketch, "E18.8.35.0", {"start": v(5.17, 39.9) * mm, "mid": v(4.67, 39.82) * mm, "end": v(4.27, 39.5) * mm});
            skArc(sketch, "E18.12.35.0", {"start": v(3.47, 38.26) * mm, "mid": v(3.85, 38.9) * mm, "end": v(4.27, 39.5) * mm});
            skPoint(sketch, "E18.16.35.0", {"position": v(5.87, 39.79) * mm});
            skPoint(sketch, "E18.17.35.0", {"position": v(6.62, 37.52) * mm});
            skPoint(sketch, "E18.18.35.0", {"position": v(3.32, 37.96) * mm});
            skPoint(sketch, "E18.19.35.0", {"position": v(4.63, 39.95) * mm});
            skArc(sketch, "E18.20.35.0", {"start": v(6.55, 37.85) * mm, "mid": v(6.35, 38.56) * mm, "end": v(6.1, 39.26) * mm});
            skArc(sketch, "E18.24.35.0", {"start": v(6.1, 39.26) * mm, "mid": v(5.8, 39.67) * mm, "end": v(5.34, 39.88) * mm});
            skArc(sketch, "E18.28.35.0", {"start": v(6.56, 37.22) * mm, "mid": v(6.59, 37.54) * mm, "end": v(6.55, 37.85) * mm});
            skArc(sketch, "E18.32.35.0", {"start": v(3.47, 38.26) * mm, "mid": v(3.35, 37.96) * mm, "end": v(3.3, 37.65) * mm});
            skLineSegment(sketch, "E18.36.35.0", {"start": v(5.17, 39.9) * mm, "end": v(5.25, 39.9) * mm});
            skLineSegment(sketch, "E18.39.35.0", {"start": v(3.3, 37.65) * mm, "end": v(3.27, 37.4) * mm});
            skLineSegment(sketch, "E18.42.35.0", {"start": v(6.56, 37.22) * mm, "end": v(6.52, 36.97) * mm});
            skLineSegment(sketch, "E18.45.35.0", {"start": v(5.34, 39.88) * mm, "end": v(5.25, 39.9) * mm});
            skSolve(sketch);
        }
        {
            var Q0;
            Q0 = qSketchRegion(id + "F3", true);
            extrude(context, id + "F4", {"entities" : qUnion([Q0]), "operationType" : NewBodyOperationType.ADD, "oppositeDirection" : true, "depth" : 6.35 * mm});
        }
        {
            var Q0;
            Q0=sQuery(id+"F3.wireOp",VERTEX,"E1.center");
            var Q1;
            Q1=makeQuery(id+"F1.opExtrude","SWEPT_BODY",BODY,{"disambiguationData":[OSD([sQuery(id+"F0.wireOp",EDGE,"E0")])]});
            hole(context, id + "F5", {"style" : HoleStyle.SIMPLE, "endStyle" : HoleEndStyle.THROUGH, "holeDiameter" : 12.7 * mm, "tappedDepth" : 12.7 * mm, "tapClearance" : 3, "locations" : qUnion([Q0]), "scope" : qUnion([Q1])});
        }
    });
